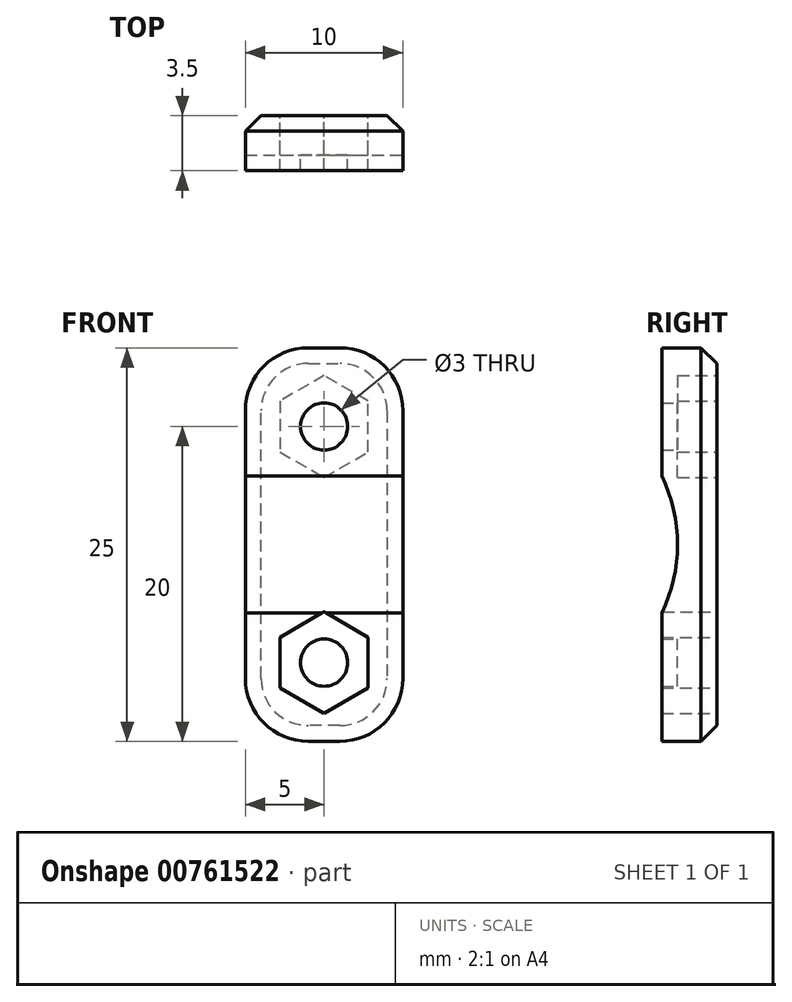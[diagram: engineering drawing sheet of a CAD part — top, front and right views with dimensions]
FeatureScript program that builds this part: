
annotation { "Feature Type Name" : "Feature", "Feature Type Description" : "" }
export const myFeature = defineFeature(function(context is Context, id is Id, definition is map)
    precondition{}
    {
        {
            var Q0;
            Q0=qCreatedBy(makeId("Front.planeOp"),FACE);
            var sketch = newSketch(context, id + "F0", { "sketchPlane" : qUnion([Q0])});
            skLineSegment(sketch, "E0.bottom", {"start": v(5, 12.5) * mm, "end": v(-5, 12.5) * mm});
            skLineSegment(sketch, "E0.top", {"start": v(5, -12.5) * mm, "end": v(-5, -12.5) * mm});
            skLineSegment(sketch, "E0.left", {"start": v(5, 12.5) * mm, "end": v(5, -12.5) * mm});
            skLineSegment(sketch, "E0.right", {"start": v(-5, 12.5) * mm, "end": v(-5, -12.5) * mm});
            skPoint(sketch, "E0.middle", {"position": v(0, 0) * mm});
            skCircle(sketch, "E1.cCircle", {"center": v(0, -7.5) * mm, "radius": 2.8 * mm, "construction": true});
            skLineSegment(sketch, "E1.0", {"start": v(2.8, -5.88) * mm, "end": v(2.8, -9.12) * mm});
            skLineSegment(sketch, "E1.1", {"start": v(2.8, -9.12) * mm, "end": v(0, -10.73) * mm});
            skLineSegment(sketch, "E1.2", {"start": v(0, -10.73) * mm, "end": v(-2.8, -9.12) * mm});
            skLineSegment(sketch, "E1.3", {"start": v(-2.8, -9.12) * mm, "end": v(-2.8, -5.88) * mm});
            skLineSegment(sketch, "E1.4", {"start": v(-2.8, -5.88) * mm, "end": v(0, -4.27) * mm});
            skLineSegment(sketch, "E1.5", {"start": v(0, -4.27) * mm, "end": v(2.8, -5.88) * mm});
            skPoint(sketch, "E1.0.midPoint", {"position": v(2.8, -7.5) * mm});
            skLineSegment(sketch, "E2.MirrorCS", {"start": v(0, 4.27) * mm, "end": v(2.8, 5.88) * mm});
            skLineSegment(sketch, "E3.MirrorCS", {"start": v(-2.8, 5.88) * mm, "end": v(0, 4.27) * mm});
            skLineSegment(sketch, "E4.MirrorCS", {"start": v(-2.8, 9.12) * mm, "end": v(-2.8, 5.88) * mm});
            skLineSegment(sketch, "E5.MirrorCS", {"start": v(0, 10.73) * mm, "end": v(-2.8, 9.12) * mm});
            skLineSegment(sketch, "E6.MirrorCS", {"start": v(2.8, 5.88) * mm, "end": v(2.8, 9.12) * mm});
            skLineSegment(sketch, "E7.MirrorCS", {"start": v(2.8, 9.12) * mm, "end": v(0, 10.73) * mm});
            skCircle(sketch, "E8.MirrorC", {"center": v(0, 7.5) * mm, "radius": 2.8 * mm, "construction": true});
            skPoint(sketch, "E9.MirrorP", {"position": v(2.8, 7.5) * mm});
            skSolve(sketch);
        }
        {
            var Q0;
            Q0=makeQuery(id+"F0.imprint","IMPRINT",FACE,{"disambiguationData":[TD([[makeQuery(id+"F0.imprint","IMPRINT",EDGE,{"derivedFrom":sQuery(id+"F0.wireOp",EDGE,"E0.bottom")}),1.0]])]});
            extrude(context, id + "F1", {"entities" : qUnion([Q0]), "depth" : 2.5 * mm, "offsetDistance" : 25 * mm});
        }
        {
            var Q0;
            Q0=makeQuery(id+"F1.opExtrude","CAP_FACE",FACE,{"disambiguationData":[OSD([sQuery(id+"F0.wireOp",EDGE,"E0.bottom"),sQuery(id+"F0.wireOp",EDGE,"E0.top"),sQuery(id+"F0.wireOp",EDGE,"E0.left"),sQuery(id+"F0.wireOp",EDGE,"E0.right"),sQuery(id+"F0.wireOp",EDGE,"E1.0"),sQuery(id+"F0.wireOp",EDGE,"E1.1"),sQuery(id+"F0.wireOp",EDGE,"E1.2"),sQuery(id+"F0.wireOp",EDGE,"E1.3"),sQuery(id+"F0.wireOp",EDGE,"E1.4"),sQuery(id+"F0.wireOp",EDGE,"E1.5"),sQuery(id+"F0.wireOp",EDGE,"E2.MirrorCS"),sQuery(id+"F0.wireOp",EDGE,"E3.MirrorCS"),sQuery(id+"F0.wireOp",EDGE,"E4.MirrorCS"),sQuery(id+"F0.wireOp",EDGE,"E5.MirrorCS"),sQuery(id+"F0.wireOp",EDGE,"E6.MirrorCS"),sQuery(id+"F0.wireOp",EDGE,"E7.MirrorCS")])],"isStart":false});
            var sketch = newSketch(context, id + "F2", { "sketchPlane" : qUnion([Q0])});
            skCircle(sketch, "E10", {"center": v(0, 7.5) * mm, "radius": 1.5 * mm});
            skCircle(sketch, "E11.MirrorC", {"center": v(0, -7.5) * mm, "radius": 1.5 * mm});
            skLineSegment(sketch, "E12.0", {"start": v(5, 12.5) * mm, "end": v(-5, 12.5) * mm});
            skLineSegment(sketch, "E13.0", {"start": v(-5, 12.5) * mm, "end": v(-5, -12.5) * mm});
            skLineSegment(sketch, "E14.0", {"start": v(5, -12.5) * mm, "end": v(-5, -12.5) * mm});
            skLineSegment(sketch, "E15.0", {"start": v(5, 12.5) * mm, "end": v(5, -12.5) * mm});
            skSolve(sketch);
        }
        {
            var Q0;
            Q0=makeQuery(id+"F2.imprint","IMPRINT",FACE,{"disambiguationData":[TD([[makeQuery(id+"F2.imprint","IMPRINT",EDGE,{"derivedFrom":sQuery(id+"F2.wireOp",EDGE,"E12.0")}),1.0]])]});
            var Q1;
            Q1=makeQuery(id+"F2.imprint","IMPRINT",FACE,{"disambiguationData":[TD([[makeQuery(id+"F2.imprint","IMPRINT",EDGE,{"derivedFrom":sQuery(id+"F2.wireOp",EDGE,"E10")}),-1.0]])]});
            var Q2;
            Q2=makeQuery(id+"F2.imprint","IMPRINT",FACE,{"disambiguationData":[TD([[makeQuery(id+"F2.imprint","IMPRINT",EDGE,{"derivedFrom":sQuery(id+"F2.wireOp",EDGE,"E11.MirrorC")}),1.0]])]});
            extrude(context, id + "F3", {"entities" : qUnion([Q0, Q1, Q2]), "operationType" : NewBodyOperationType.ADD, "depth" : 1 * mm, "offsetDistance" : 25 * mm});
        }
        {
            var Q0;
            Q0=makeQuery(id+"F3.boolean.opBoolean","MERGE",FACE,{"derivedFrom":[makeQuery(id+"F1.opExtrude","SWEPT_FACE",FACE,{"disambiguationData":[OSD([sQuery(id+"F0.wireOp",EDGE,"E0.left")])]}),makeQuery(id+"F3.opExtrude","SWEPT_FACE",FACE,{"disambiguationData":[OSD([sQuery(id+"F2.wireOp",EDGE,"E15.0")])]})]});
            var sketch = newSketch(context, id + "F4", { "sketchPlane" : qUnion([Q0])});
            skCircle(sketch, "E16", {"center": v(-12.5, 0) * mm, "radius": 10 * mm});
            skSolve(sketch);
        }
        {
            var Q0;
            Q0 = qSketchRegion(id + "F4", true);
            extrude(context, id + "F5", {"entities" : qUnion([Q0]), "operationType" : NewBodyOperationType.REMOVE, "oppositeDirection" : true, "depth" : 25 * mm, "offsetDistance" : 25 * mm});
        }
        {
            var Q0;
            Q0=makeQuery(id+"F3.boolean.opBoolean","MERGE",EDGE,{"derivedFrom":[makeQuery(id+"F1.opExtrude","SWEPT_EDGE",EDGE,{"disambiguationData":[OSD([sQuery(id+"F0.wireOp",EDGE,"E0.bottom"),sQuery(id+"F0.wireOp",EDGE,"E0.left")])]}),makeQuery(id+"F3.opExtrude","SWEPT_EDGE",EDGE,{"disambiguationData":[OSD([sQuery(id+"F2.wireOp",EDGE,"E12.0"),sQuery(id+"F2.wireOp",EDGE,"E15.0")])]})]});
            var Q1;
            Q1=makeQuery(id+"F3.boolean.opBoolean","MERGE",EDGE,{"derivedFrom":[makeQuery(id+"F1.opExtrude","SWEPT_EDGE",EDGE,{"disambiguationData":[OSD([sQuery(id+"F0.wireOp",EDGE,"E0.bottom"),sQuery(id+"F0.wireOp",EDGE,"E0.right")])]}),makeQuery(id+"F3.opExtrude","SWEPT_EDGE",EDGE,{"disambiguationData":[OSD([sQuery(id+"F2.wireOp",EDGE,"E12.0"),sQuery(id+"F2.wireOp",EDGE,"E13.0")])]})]});
            var Q2;
            Q2=makeQuery(id+"F3.boolean.opBoolean","MERGE",EDGE,{"derivedFrom":[makeQuery(id+"F1.opExtrude","SWEPT_EDGE",EDGE,{"disambiguationData":[OSD([sQuery(id+"F0.wireOp",EDGE,"E0.top"),sQuery(id+"F0.wireOp",EDGE,"E0.right")])]}),makeQuery(id+"F3.opExtrude","SWEPT_EDGE",EDGE,{"disambiguationData":[OSD([sQuery(id+"F2.wireOp",EDGE,"E13.0"),sQuery(id+"F2.wireOp",EDGE,"E14.0")])]})]});
            var Q3;
            Q3=makeQuery(id+"F3.boolean.opBoolean","MERGE",EDGE,{"derivedFrom":[makeQuery(id+"F1.opExtrude","SWEPT_EDGE",EDGE,{"disambiguationData":[OSD([sQuery(id+"F0.wireOp",EDGE,"E0.top"),sQuery(id+"F0.wireOp",EDGE,"E0.left")])]}),makeQuery(id+"F3.opExtrude","SWEPT_EDGE",EDGE,{"disambiguationData":[OSD([sQuery(id+"F2.wireOp",EDGE,"E14.0"),sQuery(id+"F2.wireOp",EDGE,"E15.0")])]})]});
            fillet(context, id + "F6", {"entities" : qUnion([Q0, Q1, Q2, Q3]), "radius" : 4 * mm, "tangentPropagation" : true, "allowEdgeOverflow" : false});
        }
        {
            var Q0;
            Q0=makeQuery(id+"F1.opExtrude","CAP_EDGE",EDGE,{"disambiguationData":[OSD([sQuery(id+"F0.wireOp",EDGE,"E0.left")])],"isStart":true});
            chamfer(context, id + "F7", {"entities" : qUnion([Q0]), "width" : 1 * mm, "tangentPropagation" : true});
        }
    });
